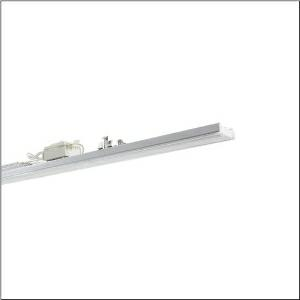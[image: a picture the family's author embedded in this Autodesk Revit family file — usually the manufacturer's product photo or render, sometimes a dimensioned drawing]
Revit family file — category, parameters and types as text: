
# Revit family: licross_11_recessed_mo_51tl12dn4axg3s4
name_source: partatom
category: Lighting Fixtures
units: mm (PartAtom-declared; Revit-internal decimal feet)

## family parameters
Cut with Voids When Loaded = No
Host = Face
Light Source = No
Part Type = Normal
Room Calculation Point = No
Round Connector Dimension = Use Diameter
Shared = No

## types (1)
- --- (1 x LED, 1010 lm, 6.7 W, 4000K)
    Apparent Load = 7 VA
    CIE Flux Codes = 67 92 99 100 100
    Color Rendering = 80
    Color Temperature = 4000K
    Default Elevation = 1800 mm
    Description = Licross 11 Recessed MO, luminaire insert, of sheet steel, coil coated, white, length: 1.500mm, width: 66mm, height: 67mm, LED rated luminous flux: 10.240lm, light colour: 840, SDCM (Standard Deviation of Colour Matching)MacAdam ≤ 2 SDCM (initial), control gear: DALI 2, with plug, 6-pole, with phase selection, for trunking rail, 9 or 11-core, mains connection: 220..240V, AC, 50/60Hz, rated input power: 61W, for trunking rail, 9-/11-core, internal wiring halogen-free, for emergency light function, converter,control gear: single battery element, battery: LiFePO4, 9Ah, primary optical cover: cover, of PMMA, light emission: direct distribution, primary light characteristic: symmetric, protection rating (complete): IP40, insulation class (complete): insulation class I (protective earthing), certification: CE, UKCA, protection symbol: D if used in an environment without relevant dust loads with corresponding accessories, impact resistance: IK06, permissible ambient temperature for indoor applications: +5..+35°C, standard: EN 60598-2-22, LABS conformity tested according to VDMA 24364:2018-05, reducing of maximum allowable ambient temperature of 5°C with ceiling mounting, corresponds to IFS (International Featured Standards) requirements for safety and quality in the food industry, The light source and the operating device comply with the requirements of the Ecodesign Regulation (EU) 2019/2020 and are replaceable in accordance with this regulation, packaging unit: 1 piece
    Height = 58 mm
    Lamp = 1 x LED
    Lamp Light Flux = 1010 lm
    Lamp Power = 6.7 W
    Lamp count = 1
    Length = 1500 mm
    Luminous efficacy = 151 lm/W
    Manufacturer = Siteco
    ModVariant = No
    Model = 51TL12DN4AXG3S4
    Mounting Place = Ceiling
    Mounting Type = Pendant
    Number of Poles = 1
    OnlyDefault = Yes
    Power Factor = 1
    Product Name = Licross 11 Recessed MO
    Product group = luminaire insert | ceiling pendant
    ProductGroupID = 901
    Protection Class = Protection class I
    Protection Degree = IP 40
    RLX_Detail_Level = 1
    RLX_Emergency_Light_Flux = 0 lm
    RLX_Emergency_Type = 0
    RLX_Emergency_Type_DB = No
    RlxData = <blob elided: 25049 chars, md5=815a433b>
    Socket = socket
    Standby Power = 0 W
    System Light Flux = 1010 lm
    System Power = 7 W
    Type Comments = : emergency light operation: 3 h
    Type Image = l_1296930.jpg
    URL = http://relux.com
    VarID = @adj_094017
    Voltage = 0 V
    Weight = 0.00 kg
    Width = 66 mm

## geometry (parser evidence)
native form markers: Blend x4, Sweep x11
no freeform markers — native parametric forms only
